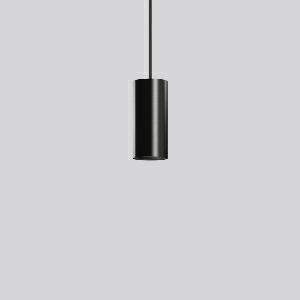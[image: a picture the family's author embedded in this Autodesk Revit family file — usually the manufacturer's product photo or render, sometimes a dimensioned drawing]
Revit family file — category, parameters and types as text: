
# Revit family: deecos_p_mini_911513_003_1_4132
name_source: partatom
category: Lighting Fixtures
units: mm (PartAtom-declared; Revit-internal decimal feet)

## family parameters
Cut with Voids When Loaded = No
Host = Face
Light Source = No
Part Type = Normal
Room Calculation Point = No
Round Connector Dimension = Use Diameter
Shared = No

## types (1)
- DEECOS P mini (1 x LED Modul 940, 2700 lm, 4000)
    Apparent Load = 20 VA
    Approval mark = CE
    CIE Flux Codes = 100 100 100 100 100
    Color Rendering = 92
    Color Temperature = 4000
    Default Elevation = 1800 mm
    Description = Series: DEECOS P mini
Cylindrical pendant luminaire. Housing: die-cast aluminium, powder-coated. Canopy made of powder-coated sheet steel with magnetic attachment. Optical assembly with reflector made of MIRO-Silver with 98% total light reflection for outstanding efficiency - can be changed without tools. Best colour rendering index Ra>90. Transparent pendant cable 5 m, can be shortened, with integrated steel cable. High quality converter without flickering and stroboscopic effect. The following accessories can be mounted without use of tools: interchangeable lenses, honeycomb louvre, clear and frosted diffusers, white interchangeable plastic ring. Decorative recessed suspension set available as accessory.Suitable for accessory Deecos P Tube cylinder extensions 0.5 m, 0.75 m or 1 m. 
Colour: deep black, matt (RAL 9005)
Diameter: 87 mm
Height: 195 mm
Suspension length: 5000 mm
Lamp: LED
Socket: without socket
Colour temperature: 4000K
Colour rendering index (CRI): 92
System power: 20 W
Rated luminous flux: 2700 lm
Luminous efficiency: 135 lm/W
Control gear: Regulated power supply
Protection class: I
Type of protection: IP 20
    Height = 195 mm
    Lamp = 1 x LED Modul 940
    Lamp Light Flux = 2700 lm
    Lamp count = 1
    Length = 87 mm
    Lifetime = 50000 h
    Luminous efficacy = 135 lm/W
    Manufacturer = RZB
    ModVariant = No
    Model = 911513.003.1
    Mounting Place = Ceiling
    Mounting Type = Pendant
    Number of Poles = 1
    OnlyDefault = Yes
    Power Factor = 1
    Product Name = DEECOS P mini
    Product group = Pendant luminaires
    ProductGroupID = 902
    Protection Class = Protection class I
    Protection Degree = IP 20
    RLX_Detail_Level = 1
    RLX_Emergency_Light_Flux = 0 lm
    RLX_Emergency_Type = 0
    RLX_Emergency_Type_DB = No
    RlxData = <blob elided: 56701 chars, md5=5a005350>
    Socket = socket
    Standby Power = 0 W
    System Light Flux = 2700 lm
    System Power = 20 W
    Type Comments = Product without accessories
    Type Image = 911476.003.jpg
    URL = http://relux.com
    VarID = ---
    Voltage = 230 V
    Voltage Range = 220-240 V
    Weight = 0.00 kg
    Width = 0 mm  [stored 0 ft]

note: [stored X ft] marks values corroborated as IEEE doubles in the binary element streams (Revit-internal decimal feet)

## geometry (parser evidence)
native form markers: Blend x4, Sweep x12
no freeform markers — native parametric forms only
